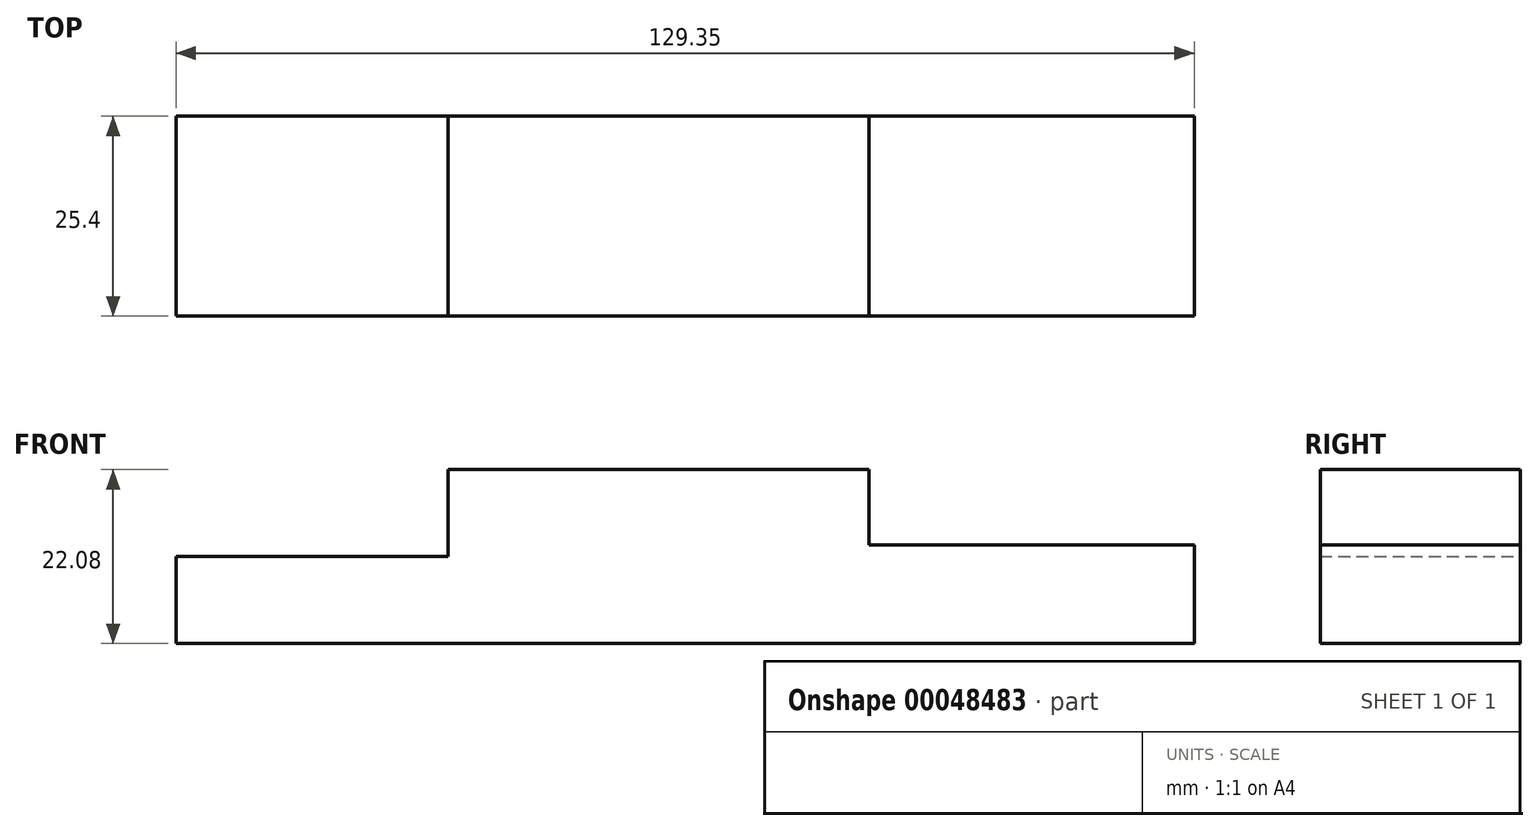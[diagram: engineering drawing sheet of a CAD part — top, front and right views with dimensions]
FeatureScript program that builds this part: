
annotation { "Feature Type Name" : "Feature", "Feature Type Description" : "" }
export const myFeature = defineFeature(function(context is Context, id is Id, definition is map)
    precondition{}
    {
        {
            var Q0;
            Q0=qCreatedBy(makeId("Front.planeOp"),FACE);
            var sketch = newSketch(context, id + "F0", { "sketchPlane" : qUnion([Q0])});
            skLineSegment(sketch, "E0.bottom", {"start": v(-22.95, 9.55) * mm, "end": v(30.5, 9.55) * mm});
            skLineSegment(sketch, "E0.top", {"start": v(-22.95, -12.52) * mm, "end": v(30.5, -12.52) * mm});
            skLineSegment(sketch, "E0.left", {"start": v(-22.95, 9.55) * mm, "end": v(-22.95, -12.52) * mm});
            skLineSegment(sketch, "E0.right", {"start": v(30.5, 9.55) * mm, "end": v(30.5, -12.52) * mm});
            skPoint(sketch, "E1.firstSnap0", {"position": v(30.5, -1.49) * mm});
            skLineSegment(sketch, "E1.bottom", {"start": v(30.5, 0) * mm, "end": v(71.82, 0) * mm});
            skLineSegment(sketch, "E1.top", {"start": v(30.5, -12.53) * mm, "end": v(71.82, -12.53) * mm});
            skLineSegment(sketch, "E1.left", {"start": v(30.5, 0) * mm, "end": v(30.5, -12.53) * mm});
            skLineSegment(sketch, "E1.right", {"start": v(71.82, 0) * mm, "end": v(71.82, -12.53) * mm});
            skLineSegment(sketch, "E2.bottom", {"start": v(-22.95, -1.49) * mm, "end": v(-57.53, -1.49) * mm});
            skLineSegment(sketch, "E2.right", {"start": v(-57.53, -1.49) * mm, "end": v(-57.53, -12.53) * mm});
            skLineSegment(sketch, "E3", {"start": v(-22.95, -12.52) * mm, "end": v(-57.53, -12.53) * mm});
            skSolve(sketch);
        }
        {
            var Q0;
            {var subQ1=sQuery(id+"F0.wireOp",EDGE,"E2.bottom");Q0=makeQuery(id+"F0.imprint","IMPRINT",FACE,{"disambiguationData":[TD([[makeQuery(id+"F0.imprint","IMPRINT",EDGE,{"derivedFrom":subQ1}),1.0]])]});}
            var Q1;
            {var subQ0=sQuery(id+"F0.wireOp",EDGE,"E1.bottom");Q1=makeQuery(id+"F0.imprint","IMPRINT",FACE,{"disambiguationData":[TD([[makeQuery(id+"F0.imprint","IMPRINT",EDGE,{"derivedFrom":subQ0}),-1.0]])]});}
            var Q2;
            {var subQ3=sQuery(id+"F0.wireOp",EDGE,"E0.bottom");Q2=makeQuery(id+"F0.imprint","IMPRINT",FACE,{"disambiguationData":[TD([[makeQuery(id+"F0.imprint","IMPRINT",EDGE,{"derivedFrom":subQ3}),-1.0]])]});}
            extrude(context, id + "F1", {"entities" : qUnion([Q0, Q1, Q2]), "depth" : 25.4 * mm});
        }
    });
